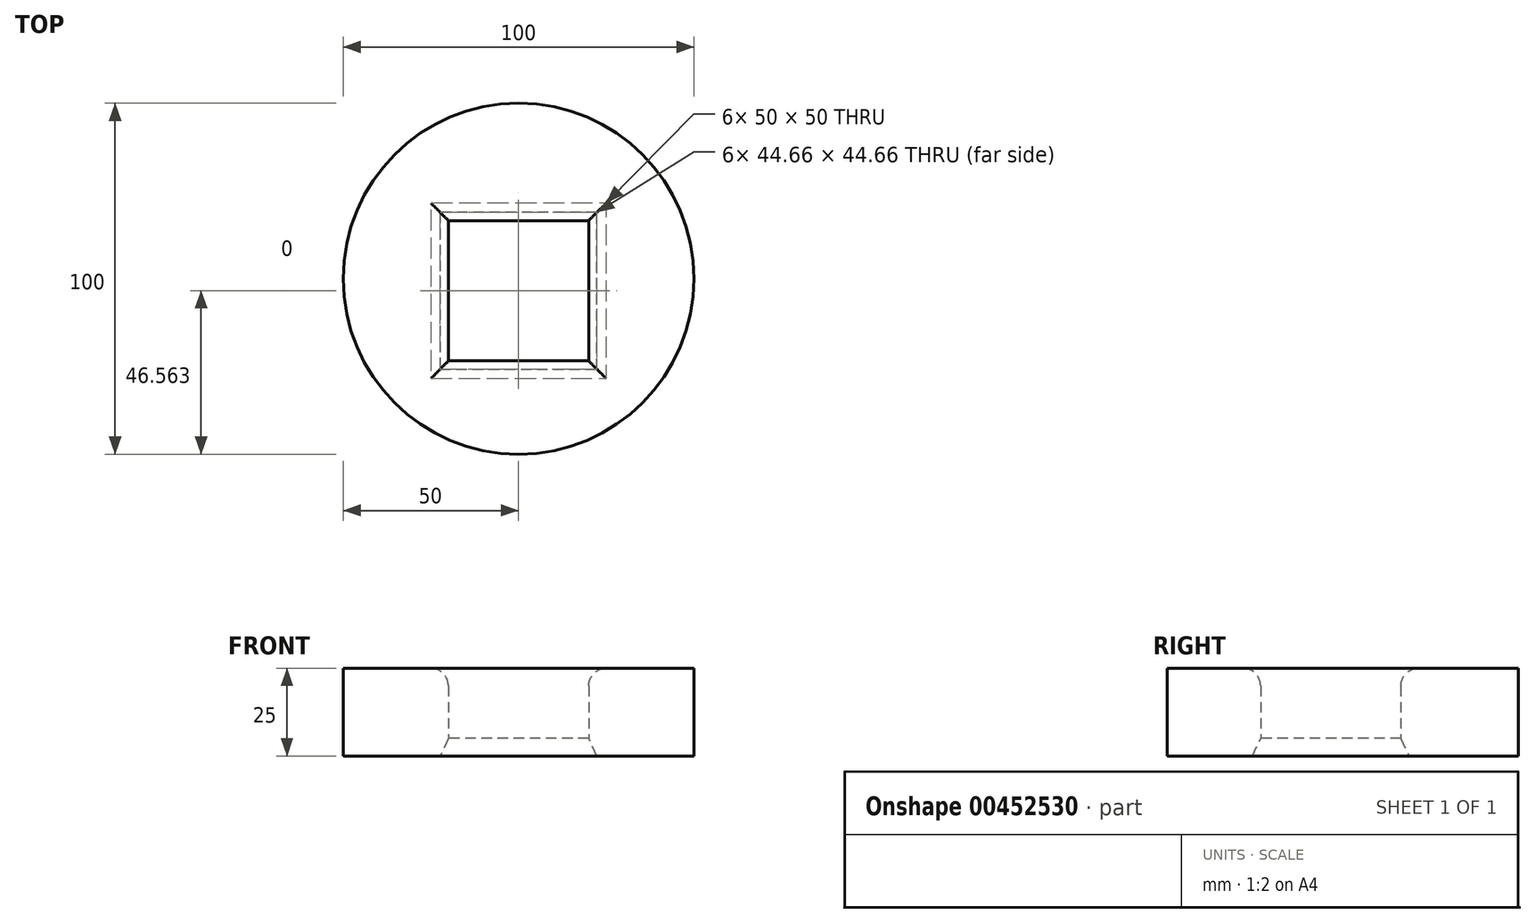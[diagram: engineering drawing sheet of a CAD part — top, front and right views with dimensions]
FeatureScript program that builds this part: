
annotation { "Feature Type Name" : "Feature", "Feature Type Description" : "" }
export const myFeature = defineFeature(function(context is Context, id is Id, definition is map)
    precondition{}
    {
        {
            var Q0;
            Q0=qCreatedBy(makeId("Top.planeOp"),FACE);
            var sketch = newSketch(context, id + "F0", { "sketchPlane" : qUnion([Q0])});
            skCircle(sketch, "E0", {"center": v(0, 0) * mm, "radius": 50 * mm});
            skLineSegment(sketch, "E1.bottom", {"start": v(20, -23.44) * mm, "end": v(-20, -23.44) * mm});
            skLineSegment(sketch, "E1.top", {"start": v(20, 16.56) * mm, "end": v(-20, 16.56) * mm});
            skLineSegment(sketch, "E1.left", {"start": v(20, -23.44) * mm, "end": v(20, 16.56) * mm});
            skLineSegment(sketch, "E1.right", {"start": v(-20, -23.44) * mm, "end": v(-20, 16.56) * mm});
            skPoint(sketch, "E1.middle", {"position": v(0, -3.44) * mm});
            skSolve(sketch);
        }
        {
            var Q0;
            Q0=makeQuery(id+"F0.imprint","IMPRINT",FACE,{"disambiguationData":[TD([[makeQuery(id+"F0.imprint","IMPRINT",EDGE,{"derivedFrom":sQuery(id+"F0.wireOp",EDGE,"E0")}),1.0]])]});
            extrude(context, id + "F1", {"entities" : qUnion([Q0]), "depth" : 25 * mm});
        }
        {
            var Q0;
            Q0=makeQuery(id+"F1.opExtrude","CAP_EDGE",EDGE,{"disambiguationData":[OSD([sQuery(id+"F0.wireOp",EDGE,"E1.top")])],"isStart":false});
            var Q1;
            Q1=makeQuery(id+"F1.opExtrude","CAP_EDGE",EDGE,{"disambiguationData":[OSD([sQuery(id+"F0.wireOp",EDGE,"E1.right")])],"isStart":false});
            var Q2;
            Q2=makeQuery(id+"F1.opExtrude","CAP_EDGE",EDGE,{"disambiguationData":[OSD([sQuery(id+"F0.wireOp",EDGE,"E1.left")])],"isStart":false});
            var Q3;
            Q3=makeQuery(id+"F1.opExtrude","CAP_EDGE",EDGE,{"disambiguationData":[OSD([sQuery(id+"F0.wireOp",EDGE,"E1.bottom")])],"isStart":false});
            fillet(context, id + "F2", {"entities" : qUnion([Q0, Q1, Q2, Q3]), "radius" : 5 * mm, "tangentPropagation" : true, "allowEdgeOverflow" : false});
        }
        {
            var Q0;
            Q0=makeQuery(id+"F1.opExtrude","CAP_EDGE",EDGE,{"disambiguationData":[OSD([sQuery(id+"F0.wireOp",EDGE,"E1.bottom")])],"isStart":true});
            var Q1;
            Q1=makeQuery(id+"F1.opExtrude","CAP_EDGE",EDGE,{"disambiguationData":[OSD([sQuery(id+"F0.wireOp",EDGE,"E1.right")])],"isStart":true});
            var Q2;
            Q2=makeQuery(id+"F1.opExtrude","CAP_EDGE",EDGE,{"disambiguationData":[OSD([sQuery(id+"F0.wireOp",EDGE,"E1.top")])],"isStart":true});
            var Q3;
            Q3=makeQuery(id+"F1.opExtrude","CAP_EDGE",EDGE,{"disambiguationData":[OSD([sQuery(id+"F0.wireOp",EDGE,"E1.left")])],"isStart":true});
            chamfer(context, id + "F3", {"entities" : qUnion([Q0, Q1, Q2, Q3]), "chamferType" : ChamferType.OFFSET_ANGLE, "width" : 5 * mm, "oppositeDirection" : false, "angle" : 25 * degree, "tangentPropagation" : true});
        }
    });
